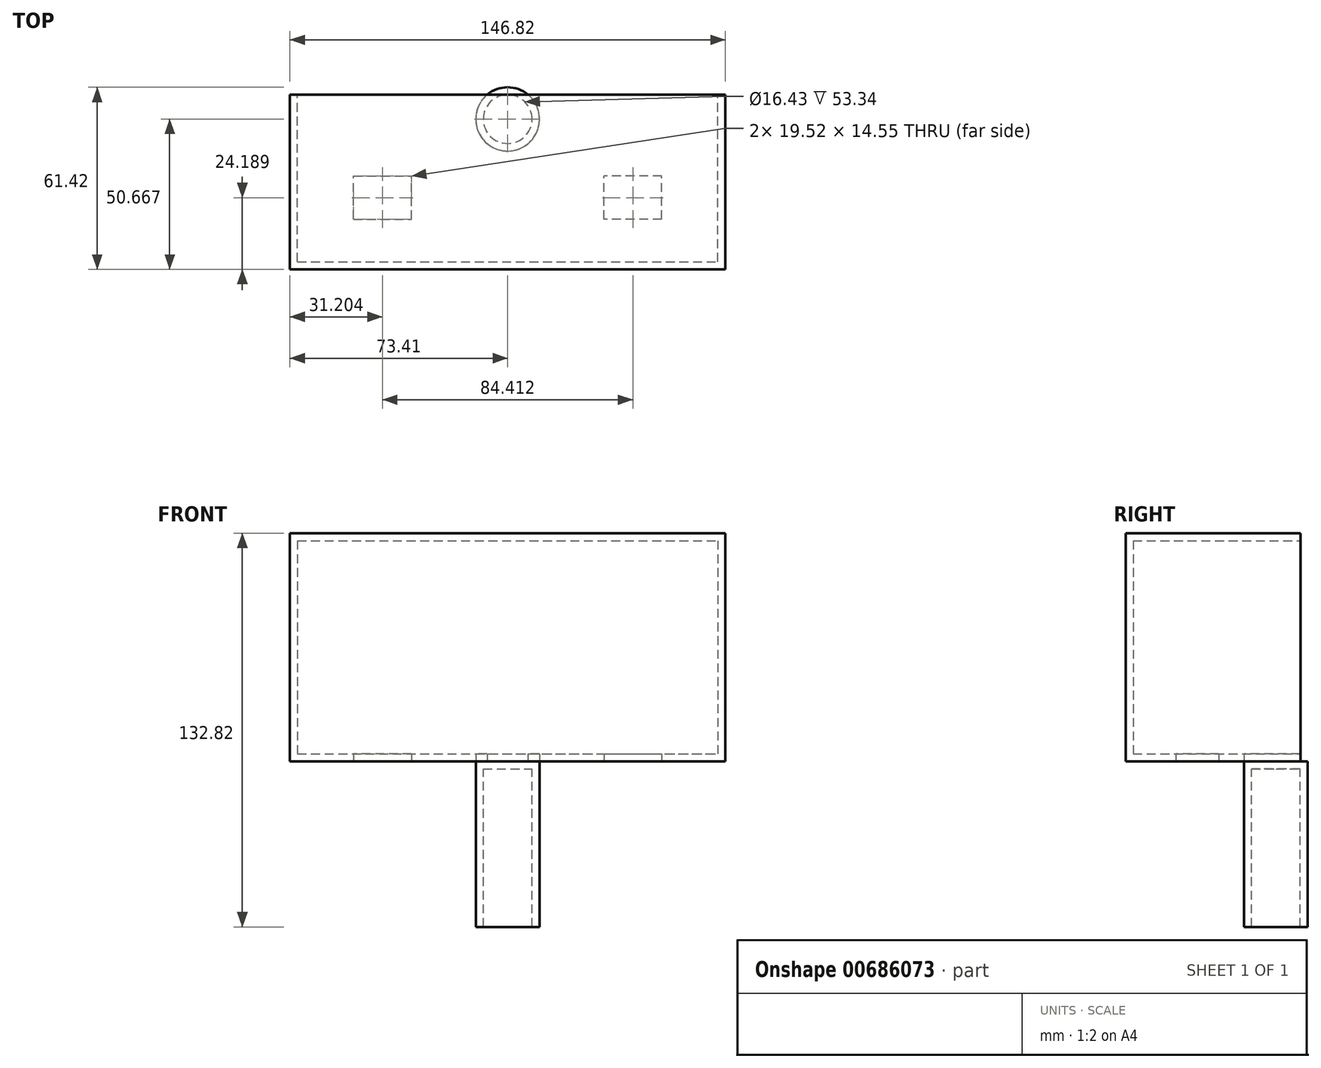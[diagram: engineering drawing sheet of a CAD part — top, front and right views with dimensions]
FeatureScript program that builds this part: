
annotation { "Feature Type Name" : "Feature", "Feature Type Description" : "" }
export const myFeature = defineFeature(function(context is Context, id is Id, definition is map)
    precondition{}
    {
        {
            var Q0;
            Q0=qCreatedBy(makeId("Front.planeOp"),FACE);
            var sketch = newSketch(context, id + "F0", { "sketchPlane" : qUnion([Q0])});
            skLineSegment(sketch, "E0", {"start": v(-7.56, -16.17) * mm, "end": v(-7.56, -63.84) * mm});
            skLineSegment(sketch, "E1", {"start": v(5.65, -16.17) * mm, "end": v(5.65, -63.84) * mm});
            skLineSegment(sketch, "E2.bottom", {"start": v(-73.4, 60.77) * mm, "end": v(73.4, 60.77) * mm});
            skLineSegment(sketch, "E2.top", {"start": v(-73.4, -16.17) * mm, "end": v(-7.56, -16.17) * mm});
            skLineSegment(sketch, "E2.left", {"start": v(-73.4, 60.77) * mm, "end": v(-73.4, -16.17) * mm});
            skLineSegment(sketch, "E2.right", {"start": v(73.4, 60.77) * mm, "end": v(73.4, -16.17) * mm});
            skLineSegment(sketch, "E3.trimOffspring", {"start": v(5.65, -16.17) * mm, "end": v(73.4, -16.17) * mm});
            skPoint(sketch, "E4.orphan", {"position": v(5.65, 0) * mm});
            skPoint(sketch, "E5.orphan", {"position": v(-7.56, 0) * mm});
            skArc(sketch, "E6", {"start": v(5.65, -16.17) * mm, "mid": v(-0.96, 0.05) * mm, "end": v(-7.56, -16.17) * mm});
            skLineSegment(sketch, "E7", {"start": v(-7.56, -16.17) * mm, "end": v(5.65, -16.17) * mm});
            skSolve(sketch);
        }
        {
            var Q0;
            Q0=makeQuery(id+"F0.imprint","IMPRINT",FACE,{"disambiguationData":[TD([[makeQuery(id+"F0.imprint","IMPRINT",EDGE,{"derivedFrom":sQuery(id+"F0.wireOp",EDGE,"E2.bottom")}),-1.0]])]});
            var Q1;
            Q1=makeQuery(id+"F0.imprint","IMPRINT",FACE,{"disambiguationData":[TD([[makeQuery(id+"F0.imprint","IMPRINT",EDGE,{"derivedFrom":sQuery(id+"F0.wireOp",EDGE,"E6")}),1.0]])]});
            extrude(context, id + "F1", {"entities" : qUnion([Q0, Q1]), "depth" : 58.93 * mm, "offsetDistance" : 25.4 * mm});
        }
        {
            var Q0;
            Q0=makeQuery(id+"F1.opExtrude","CAP_FACE",FACE,{"disambiguationData":[OSD([sQuery(id+"F0.wireOp",EDGE,"E2.bottom"),sQuery(id+"F0.wireOp",EDGE,"E2.top"),sQuery(id+"F0.wireOp",EDGE,"E2.left"),sQuery(id+"F0.wireOp",EDGE,"E2.right"),sQuery(id+"F0.wireOp",EDGE,"E3.trimOffspring"),sQuery(id+"F0.wireOp",EDGE,"E7")])],"isStart":true});
            shell(context, id + "F2", {"entities" : qUnion([Q0]), "thickness" : 2.54 * mm});
        }
        {
            var Q0;
            Q0=makeQuery(id+"F1.opExtrude","SWEPT_FACE",FACE,{"disambiguationData":[OSD([sQuery(id+"F0.wireOp",EDGE,"E2.top"),sQuery(id+"F0.wireOp",EDGE,"E3.trimOffspring"),sQuery(id+"F0.wireOp",EDGE,"E7")])]});
            var sketch = newSketch(context, id + "F3", { "sketchPlane" : qUnion([Q0])});
            skCircle(sketch, "E8", {"center": v(0, 8.26) * mm, "radius": 10.75 * mm});
            skSolve(sketch);
        }
        {
            var Q0;
            Q0 = qSketchRegion(id + "F3", true);
            extrude(context, id + "F4", {"entities" : qUnion([Q0]), "operationType" : NewBodyOperationType.REMOVE, "oppositeDirection" : true, "depth" : 33.53 * mm, "offsetDistance" : 25.4 * mm});
        }
        {
            var Q0;
            Q0 = qSketchRegion(id + "F3", true);
            extrude(context, id + "F5", {"entities" : qUnion([Q0]), "depth" : 55.88 * mm, "offsetDistance" : 25.4 * mm});
        }
        {
            var Q0;
            Q0=makeQuery(id+"F5.opExtrude","CAP_FACE",FACE,{"disambiguationData":[OSD([sQuery(id+"F3.wireOp",EDGE,"E8")])],"isStart":false});
            shell(context, id + "F6", {"entities" : qUnion([Q0]), "thickness" : 2.54 * mm});
        }
        {
            var Q0;
            Q0=makeQuery(id+"F1.opExtrude","SWEPT_FACE",FACE,{"disambiguationData":[OSD([sQuery(id+"F0.wireOp",EDGE,"E2.top"),sQuery(id+"F0.wireOp",EDGE,"E3.trimOffspring"),sQuery(id+"F0.wireOp",EDGE,"E7")])]});
            var sketch = newSketch(context, id + "F7", { "sketchPlane" : qUnion([Q0])});
            skLineSegment(sketch, "E9.bottom", {"start": v(-51.97, 42.01) * mm, "end": v(-32.44, 42.01) * mm});
            skLineSegment(sketch, "E9.top", {"start": v(-51.97, 27.47) * mm, "end": v(-32.44, 27.47) * mm});
            skLineSegment(sketch, "E9.left", {"start": v(-51.97, 42.01) * mm, "end": v(-51.97, 27.47) * mm});
            skLineSegment(sketch, "E9.right", {"start": v(-32.44, 42.01) * mm, "end": v(-32.44, 27.47) * mm});
            skLineSegment(sketch, "E10", {"start": v(0, 51.2) * mm, "end": v(0, 23.64) * mm});
            skLineSegment(sketch, "E11.MirrorCS", {"start": v(51.97, 42.01) * mm, "end": v(32.44, 42.01) * mm});
            skLineSegment(sketch, "E12.MirrorCS", {"start": v(32.44, 42.01) * mm, "end": v(32.44, 27.47) * mm});
            skLineSegment(sketch, "E13.MirrorCS", {"start": v(51.97, 27.47) * mm, "end": v(32.44, 27.47) * mm});
            skLineSegment(sketch, "E14.MirrorCS", {"start": v(51.97, 42.01) * mm, "end": v(51.97, 27.47) * mm});
            skSolve(sketch);
        }
        {
            var Q0;
            Q0=makeQuery(id+"F7.imprint","IMPRINT",FACE,{"disambiguationData":[TD([[makeQuery(id+"F7.imprint","IMPRINT",EDGE,{"derivedFrom":sQuery(id+"F7.wireOp",EDGE,"E11.MirrorCS")}),1.0]])]});
            var Q1;
            Q1=makeQuery(id+"F7.imprint","IMPRINT",FACE,{"disambiguationData":[TD([[makeQuery(id+"F7.imprint","IMPRINT",EDGE,{"derivedFrom":sQuery(id+"F7.wireOp",EDGE,"E9.bottom")}),-1.0]])]});
            extrude(context, id + "F8", {"entities" : qUnion([Q0, Q1]), "operationType" : NewBodyOperationType.REMOVE, "oppositeDirection" : true, "depth" : 31.5 * mm, "offsetDistance" : 25.4 * mm});
        }
    });
